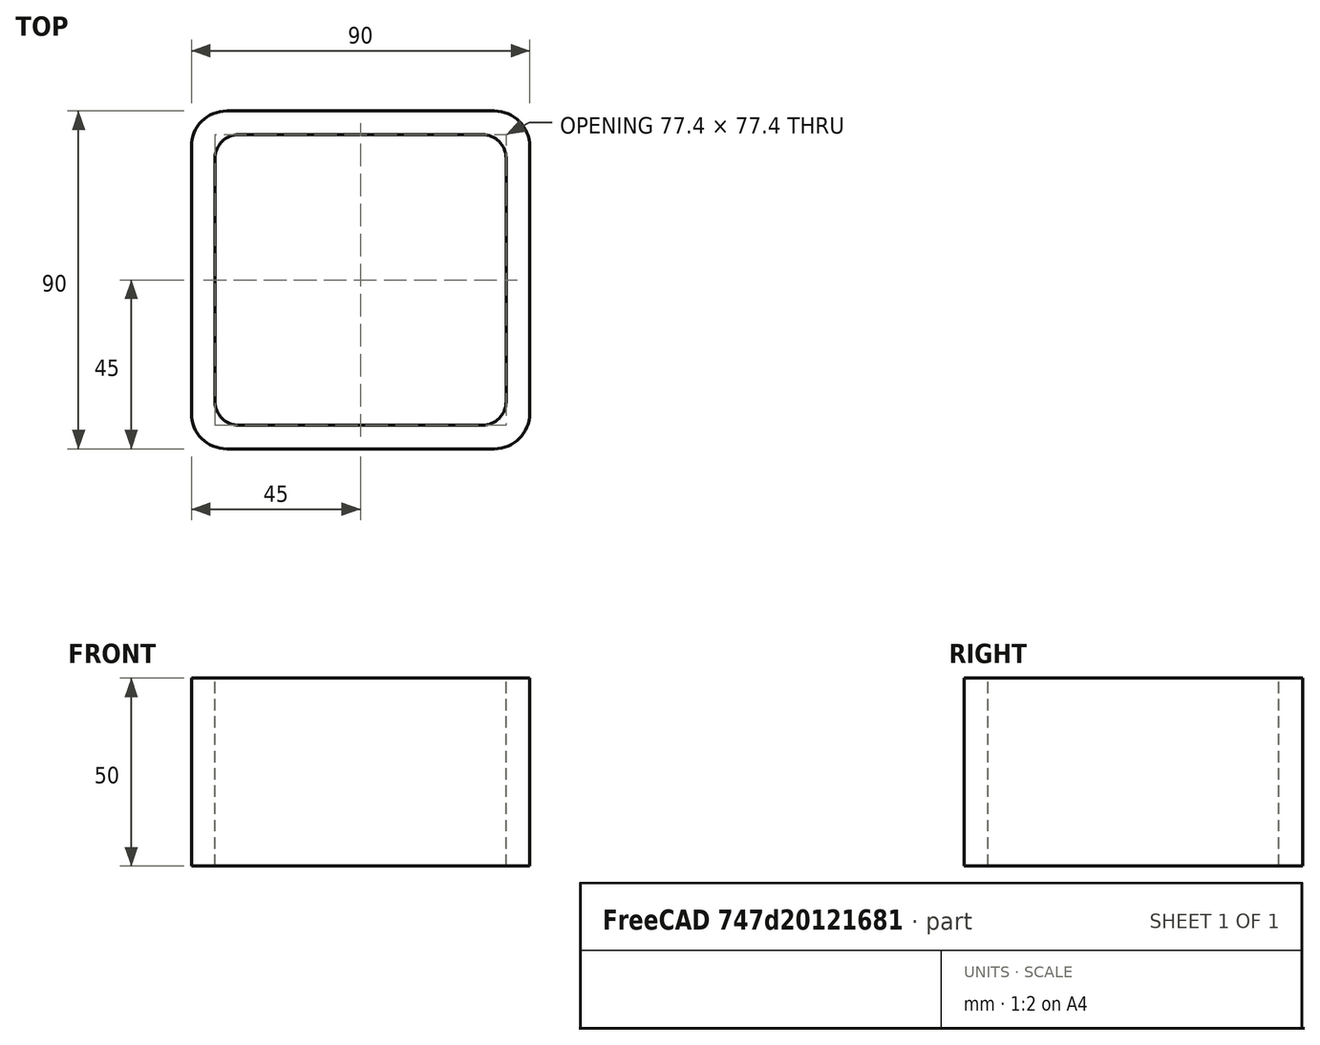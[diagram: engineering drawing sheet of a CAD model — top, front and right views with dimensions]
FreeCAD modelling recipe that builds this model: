
FCSTD DOCUMENT  (FreeCAD 0.15R4671 (Git))
Label: Square hollow section 90x90x6.3 EN10219 S235JRH
License: All rights reserved
LicenseURL: http://en.wikipedia.org/wiki/All_rights_reserved
objects: Sketcher::SketchObject×1, Part::Extrusion×1
note: 2 computed .brp shape members not serialized (recipe doc carries the construction recipe); baked Part::Feature solids carry a one-line shape summary decoded from their .brp

FEATURE [Sketcher::SketchObject] Sketch
  sketch-geometry (16):
    g0: LineSegment StartX=-32.4 StartY=38.7 StartZ=0 EndX=32.4 EndY=38.7 EndZ=0
    g1: LineSegment StartX=38.7 StartY=32.4 StartZ=0 EndX=38.7 EndY=-32.4 EndZ=0
    g2: LineSegment StartX=32.4 StartY=-38.7 StartZ=0 EndX=-32.4 EndY=-38.7 EndZ=0
    g3: LineSegment StartX=-38.7 StartY=-32.4 StartZ=0 EndX=-38.7 EndY=32.4 EndZ=0
    g4: LineSegment StartX=-35.55 StartY=45 StartZ=0 EndX=35.55 EndY=45 EndZ=0
    g5: LineSegment StartX=45 StartY=35.55 StartZ=0 EndX=45 EndY=-35.55 EndZ=0
    g6: LineSegment StartX=35.55 StartY=-45 StartZ=0 EndX=-35.55 EndY=-45 EndZ=0
    g7: LineSegment StartX=-45 StartY=-35.55 StartZ=0 EndX=-45 EndY=35.55 EndZ=0
    g8: ArcOfCircle CenterX=-32.4 CenterY=32.4 CenterZ=0 NormalX=0 NormalY=0 NormalZ=1 Radius=6.3 StartAngle=1.5708 EndAngle=3.14159
    g9: ArcOfCircle CenterX=32.4 CenterY=32.4 CenterZ=0 NormalX=0 NormalY=0 NormalZ=1 Radius=6.3 StartAngle=0 EndAngle=1.5708
    g10: ArcOfCircle CenterX=32.4 CenterY=-32.4 CenterZ=0 NormalX=0 NormalY=0 NormalZ=1 Radius=6.3 StartAngle=4.71239 EndAngle=6.28319
    g11: ArcOfCircle CenterX=-32.4 CenterY=-32.4 CenterZ=0 NormalX=0 NormalY=0 NormalZ=1 Radius=6.3 StartAngle=3.14159 EndAngle=4.71239
    g12: ArcOfCircle CenterX=35.55 CenterY=35.55 CenterZ=0 NormalX=0 NormalY=0 NormalZ=1 Radius=9.45 StartAngle=0 EndAngle=1.5708
    g13: ArcOfCircle CenterX=35.55 CenterY=-35.55 CenterZ=0 NormalX=0 NormalY=0 NormalZ=1 Radius=9.45 StartAngle=4.71239 EndAngle=6.28319
    g14: ArcOfCircle CenterX=-35.55 CenterY=-35.55 CenterZ=0 NormalX=0 NormalY=0 NormalZ=1 Radius=9.45 StartAngle=3.14159 EndAngle=4.71239
    g15: ArcOfCircle CenterX=-35.55 CenterY=35.55 CenterZ=0 NormalX=0 NormalY=0 NormalZ=1 Radius=9.45 StartAngle=1.5708 EndAngle=3.14159
  constraints (36):
    c: Horizontal(g2)
    c: Vertical(g3)
    c: Horizontal(g6)
    c: Vertical(g7)
    c: Tangent(g3,g8) = 1.5708
    c: Tangent(g0,g8) = 1.5708
    c: Tangent(g0,g9) = 1.5708
    c: Tangent(g1,g9) = 1.5708
    c: Tangent(g1,g10) = 1.5708
    c: Tangent(g2,g10) = 1.5708
    c: Tangent(g2,g11) = 1.5708
    c: Tangent(g3,g11) = 1.5708
    c: Tangent(g4,g12) = 1.5708
    c: Tangent(g5,g12) = 1.5708
    c: Tangent(g5,g13) = 1.5708
    c: Tangent(g6,g13) = 1.5708
    c: Tangent(g6,g14) = 1.5708
    c: Tangent(g7,g14) = 1.5708
    c: Tangent(g7,g15) = 1.5708
    c: Tangent(g4,g15) = 1.5708
    c: Equal(g9,g8)
    c: Equal(g9,g11)
    c: Equal(g9,g10)
    c: Equal(g12,g15)
    c: Equal(g12,g14)
    c: Equal(g12,g13)
    c: Symmetric(g4,g6,g-1)
    c: Symmetric(g7,g5,g-2)
    c: DistanceY(g4,g6) = -90
    c: DistanceX(g7,g5) = 90
    c: Symmetric(g3,g1,g-2)
    c: Symmetric(g0,g2,g-1)
    c: DistanceY(g0,g4) = 6.3
    c: DistanceX(g5,g1) = -6.3
    c: Radius(g9) = 6.3
    c: Radius(g12) = 9.45
FEATURE [Part::Extrusion] Extrude  label="Square hollow section 90x90x6.3 EN10219 S235JRH"
  Base = -> Sketch
  Dir = (0,0,50)
  Solid = true
